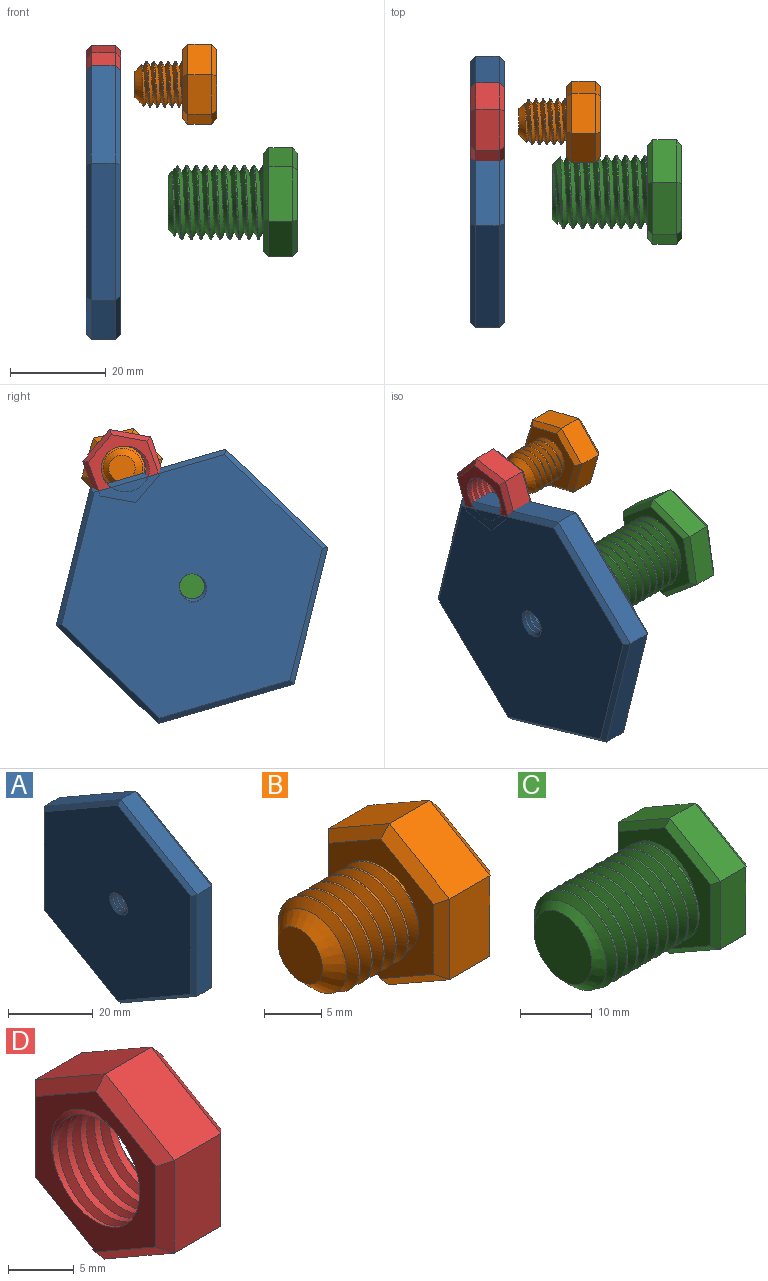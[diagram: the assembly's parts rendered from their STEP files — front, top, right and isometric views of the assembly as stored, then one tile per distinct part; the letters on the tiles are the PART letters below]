
ASSEMBLY  parts=4 mates=2
PART A: 23 faces, bbox 8.4x51.4x59.3 mm
  f0: cylinder r=2.61mm len=7mm, axis (1,0,0), area 39.6mm2, adj f7,f8,f21,f22
  f1: plane 25.48x14.75mm, normal (0,-0.5,0.87), area 147.2mm2, adj f2,f6,f14,f18
  f2: plane 29.45x5mm, normal (0,-1,0), area 147.2mm2, adj f1,f3,f12,f16
  f3: plane 25.52x14.69mm, normal (0,-0.5,-0.87), area 147.2mm2, adj f2,f4,f10,f15
  f4: plane 25.48x14.75mm, normal (0,0.5,-0.87), area 147.2mm2, adj f3,f5,f9,f17
  f5: plane 29.45x5mm, normal (0,1,0), area 147.2mm2, adj f4,f6,f11,f19
  f6: plane 25.52x14.69mm, normal (0,0.5,0.87), area 147.2mm2, adj f1,f5,f13,f20
  f7: plane 56.96x49.42mm, normal (-1,0,0), area 2053.7mm2, adj f0,f9,f10,f11,f12,f13,f14,f21
  f8: plane 56.97x49.42mm, normal (1,0,0), area 2053.7mm2, adj f0,f15,f16,f17,f18,f19,f20,f21
  f9: plane 25.48x15.33mm, normal (-0.71,0.35,-0.61), area 40.8mm2, adj f4,f7,f10,f11
  f10: plane 25.52x15.27mm, normal (-0.71,-0.35,-0.61), area 40.8mm2, adj f3,f7,f9,f12
  f11: plane 29.45x1.04mm, normal (-0.71,0.71,0), area 40.8mm2, adj f5,f7,f9,f13
  f12: plane 29.45x1.04mm, normal (-0.71,-0.71,0), area 40.8mm2, adj f2,f7,f10,f14
  f13: plane 25.52x15.27mm, normal (-0.71,0.35,0.61), area 40.8mm2, adj f6,f7,f11,f14
  f14: plane 25.48x15.33mm, normal (-0.71,-0.35,0.61), area 40.8mm2, adj f1,f7,f12,f13
  f15: plane 25.52x15.27mm, normal (0.71,-0.35,-0.61), area 40.8mm2, adj f3,f8,f16,f17
  f16: plane 29.45x1.04mm, normal (0.71,-0.71,0), area 40.8mm2, adj f2,f8,f15,f18
  f17: plane 25.48x15.33mm, normal (0.71,0.35,-0.61), area 40.8mm2, adj f4,f8,f15,f19
  f18: plane 25.48x15.33mm, normal (0.71,-0.35,0.61), area 40.8mm2, adj f1,f8,f16,f20
  f19: plane 29.45x1.04mm, normal (0.71,0.71,0), area 40.8mm2, adj f5,f8,f17,f20
  f20: plane 25.52x15.27mm, normal (0.71,0.35,0.61), area 40.8mm2, adj f6,f8,f18,f19
  f21: bspline ~8.03x7.69mm, area 85.1mm2, adj f0,f7,f8,f22
  f22: bspline ~8.03x7.69mm, area 85.1mm2, adj f0,f7,f8,f21
PART B: 25 faces, bbox 17.8x15.9x18.1 mm
  f0: cylinder r=4.75mm len=9.5mm, axis (1,0,0), area 28.1mm2, adj f1,f2,f4,f12
  f1: bspline ~10.97x9.91mm, area 196.7mm2, adj f0,f2,f4,f12
  f2: bspline ~10.97x10.66mm, area 196.6mm2, adj f0,f1,f4,f12
  f3: plane 5.5x5.5mm, normal (-1,0,0), area 23.8mm2, adj f4
  f4: cone r=4.75mm half-angle=45deg, axis (1,0,0), area 47.4mm2, adj f0,f1,f2,f3
  f5: plane 7.48x5mm, normal (0,-0.5,0.86), area 43.3mm2, adj f6,f10,f18,f22
  f6: plane 8.66x5mm, normal (0,-1,0), area 43.3mm2, adj f5,f7,f16,f20
  f7: plane 7.52x5mm, normal (0,-0.5,-0.87), area 43.3mm2, adj f6,f8,f14,f19
  f8: plane 7.48x5mm, normal (0,0.5,-0.86), area 43.3mm2, adj f7,f9,f13,f21
  f9: plane 8.66x5mm, normal (0,1,0), area 43.3mm2, adj f8,f10,f15,f23
  f10: plane 7.52x5mm, normal (0,0.5,0.87), area 43.3mm2, adj f5,f9,f17,f24
  f11: plane 15.01x13.03mm, normal (1,0,0), area 146.4mm2, adj f13,f14,f15,f16,f17,f18
  f12: plane 15.83x13.85mm, normal (-1,0,0), area 89.2mm2, adj f0,f1,f2,f19,f20,f21,f22,f23
  f13: plane 7.49x4.93mm, normal (0.71,0.36,-0.61), area 11.4mm2, adj f8,f11,f14,f15
  f14: plane 7.52x4.88mm, normal (0.71,-0.35,-0.61), area 11.4mm2, adj f7,f11,f13,f16
  f15: plane 8.66x1.03mm, normal (0.71,0.71,0), area 11.4mm2, adj f9,f11,f13,f17
  f16: plane 8.66x1.03mm, normal (0.71,-0.71,0), area 11.4mm2, adj f6,f11,f14,f18
  f17: plane 7.52x4.88mm, normal (0.71,0.35,0.61), area 11.4mm2, adj f10,f11,f15,f18
  f18: plane 7.49x4.93mm, normal (0.71,-0.36,0.61), area 11.4mm2, adj f5,f11,f16,f17
  f19: plane 7.52x4.88mm, normal (-0.71,-0.35,-0.61), area 11.4mm2, adj f7,f12,f20,f21
  f20: plane 8.66x1.03mm, normal (-0.71,-0.71,0), area 11.4mm2, adj f6,f12,f19,f22
  f21: plane 7.49x4.93mm, normal (-0.71,0.36,-0.61), area 11.4mm2, adj f8,f12,f19,f23
  f22: plane 7.49x4.93mm, normal (-0.71,-0.36,0.61), area 11.4mm2, adj f5,f12,f20,f24
  f23: plane 8.66x1.03mm, normal (-0.71,0.71,0), area 11.4mm2, adj f9,f12,f21,f24
  f24: plane 7.52x4.88mm, normal (-0.71,0.35,0.61), area 11.4mm2, adj f10,f12,f22,f23
PART C: 26 faces, bbox 27.7x20x23.1 mm
  f0: cylinder r=7.68mm len=18mm, axis (1,0,0), area 139.1mm2, adj f1,f2,f5,f13
  f1: bspline ~20.88x17.74mm, area 713.8mm2, adj f0,f2,f4,f5,f13
  f2: bspline ~21.88x17.74mm, area 715.1mm2, adj f0,f1,f4,f5,f13
  f3: plane 11.36x11.36mm, normal (-1,0,0), area 101.4mm2, adj f4
  f4: cone r=7.68mm half-angle=45deg, axis (1,0,0), area 63.2mm2, adj f1,f2,f3,f5
  f5: cone r=7.68mm half-angle=45deg, axis (1,0,0), area 13.2mm2, adj f0,f1,f2,f4
  f6: plane 9.98x5.81mm, normal (0,-0.5,0.86), area 57.7mm2, adj f7,f11,f19,f23
  f7: plane 11.55x5mm, normal (0,-1,0), area 57.7mm2, adj f6,f8,f17,f21
  f8: plane 10.02x5.74mm, normal (0,-0.5,-0.87), area 57.7mm2, adj f7,f9,f15,f20
  f9: plane 9.98x5.81mm, normal (0,0.5,-0.86), area 57.7mm2, adj f8,f10,f14,f22
  f10: plane 11.55x5mm, normal (0,1,0), area 57.7mm2, adj f9,f11,f16,f24
  f11: plane 10.02x5.74mm, normal (0,0.5,0.87), area 57.7mm2, adj f6,f10,f18,f25
  f12: plane 20.78x18.04mm, normal (1,0,0), area 280.6mm2, adj f14,f15,f16,f17,f18,f19
  f13: plane 20.78x18.04mm, normal (-1,0,0), area 125.2mm2, adj f0,f1,f2,f20,f21,f22,f23,f24
  f14: plane 9.98x6.38mm, normal (0.71,0.36,-0.61), area 15.5mm2, adj f9,f12,f15,f16
  f15: plane 10.02x6.32mm, normal (0.71,-0.35,-0.61), area 15.5mm2, adj f8,f12,f14,f17
  f16: plane 11.55x1.04mm, normal (0.71,0.71,0), area 15.5mm2, adj f10,f12,f14,f18
  f17: plane 11.55x1.04mm, normal (0.71,-0.71,0), area 15.5mm2, adj f7,f12,f15,f19
  f18: plane 10.02x6.32mm, normal (0.71,0.35,0.61), area 15.5mm2, adj f11,f12,f16,f19
  f19: plane 9.98x6.38mm, normal (0.71,-0.36,0.61), area 15.5mm2, adj f6,f12,f17,f18
  f20: plane 10.02x6.32mm, normal (-0.71,-0.35,-0.61), area 15.5mm2, adj f8,f13,f21,f22
  f21: plane 11.55x1.04mm, normal (-0.71,-0.71,0), area 15.5mm2, adj f7,f13,f20,f23
  f22: plane 9.98x6.38mm, normal (-0.71,0.36,-0.61), area 15.5mm2, adj f9,f13,f20,f24
  f23: plane 9.98x6.38mm, normal (-0.71,-0.36,0.61), area 15.5mm2, adj f6,f13,f21,f25
  f24: plane 11.55x1.04mm, normal (-0.71,0.71,0), area 15.5mm2, adj f10,f13,f22,f25
  f25: plane 10.02x6.32mm, normal (-0.71,0.35,0.61), area 15.5mm2, adj f11,f13,f23,f24
PART D: 23 faces, bbox 9.1x15.4x17.7 mm
  f0: plane 7.49x5mm, normal (0,-0.5,0.86), area 43.3mm2, adj f1,f5,f13,f17
  f1: plane 8.66x5mm, normal (0,-1,0), area 43.3mm2, adj f0,f2,f11,f15
  f2: plane 7.51x5mm, normal (0,-0.5,-0.87), area 43.3mm2, adj f1,f3,f9,f14
  f3: plane 7.49x5mm, normal (0,0.5,-0.86), area 43.3mm2, adj f2,f4,f8,f16
  f4: plane 8.66x5mm, normal (0,1,0), area 43.3mm2, adj f3,f5,f10,f18
  f5: plane 7.51x5mm, normal (0,0.5,0.87), area 43.3mm2, adj f0,f4,f12,f19
  f6: plane 15.37x13.38mm, normal (-1,0,0), area 71.4mm2, adj f8,f9,f10,f11,f12,f13,f20,f21
  f7: plane 15.37x13.38mm, normal (1,0,0), area 71.4mm2, adj f14,f15,f16,f17,f18,f19,f20,f21
  f8: plane 7.49x4.93mm, normal (-0.71,0.36,-0.61), area 11.4mm2, adj f3,f6,f9,f10
  f9: plane 7.51x4.89mm, normal (-0.71,-0.35,-0.61), area 11.4mm2, adj f2,f6,f8,f11
  f10: plane 8.66x1.02mm, normal (-0.71,0.71,0), area 11.4mm2, adj f4,f6,f8,f12
  f11: plane 8.66x1.02mm, normal (-0.71,-0.71,0), area 11.4mm2, adj f1,f6,f9,f13
  f12: plane 7.51x4.89mm, normal (-0.71,0.35,0.61), area 11.4mm2, adj f5,f6,f10,f13
  f13: plane 7.49x4.93mm, normal (-0.71,-0.36,0.61), area 11.4mm2, adj f0,f6,f11,f12
  f14: plane 7.51x4.89mm, normal (0.71,-0.35,-0.61), area 11.4mm2, adj f2,f7,f15,f16
  f15: plane 8.66x1.02mm, normal (0.71,-0.71,0), area 11.4mm2, adj f1,f7,f14,f17
  f16: plane 7.49x4.93mm, normal (0.71,0.36,-0.61), area 11.4mm2, adj f3,f7,f14,f18
  f17: plane 7.49x4.93mm, normal (0.71,-0.36,0.61), area 11.4mm2, adj f0,f7,f15,f19
  f18: plane 8.66x1.02mm, normal (0.71,0.71,0), area 11.4mm2, adj f4,f7,f16,f19
  f19: plane 7.51x4.89mm, normal (0.71,0.35,0.61), area 11.4mm2, adj f5,f7,f17,f18
  f20: cylinder r=4.66mm len=9.32mm, axis (1,0,0), area 85.4mm2, adj f6,f7,f21,f22
  f21: bspline ~12.5x10.82mm, area 128.4mm2, adj f6,f7,f20,f22
  f22: bspline ~12.5x10.82mm, area 128.5mm2, adj f6,f7,f20,f21
PLACE A rot(axis=(0,0.6,-0.8),180deg) t=(-55.27,-6.86,23.48)mm fixed
PLACE B rot(axis=(-1,0,0),43.8deg) t=(-31.66,7.73,48.08)mm
PLACE C rot(axis=(1,0,0),109.9deg) t=(-14.77,-6.86,23.48)mm
PLACE D rot(axis=(1,0,0),100.2deg) t=(-48.16,7.38,48.02)mm fixed
MATE cylindrical C.f0 <-> A.f0  axis (-1,0,0) through (-38.27,-6.86,23.48)mm
MATE cylindrical B.f0 <-> D.f6  axis (-1,0,0) through (-45.16,7.73,48.08)mm
